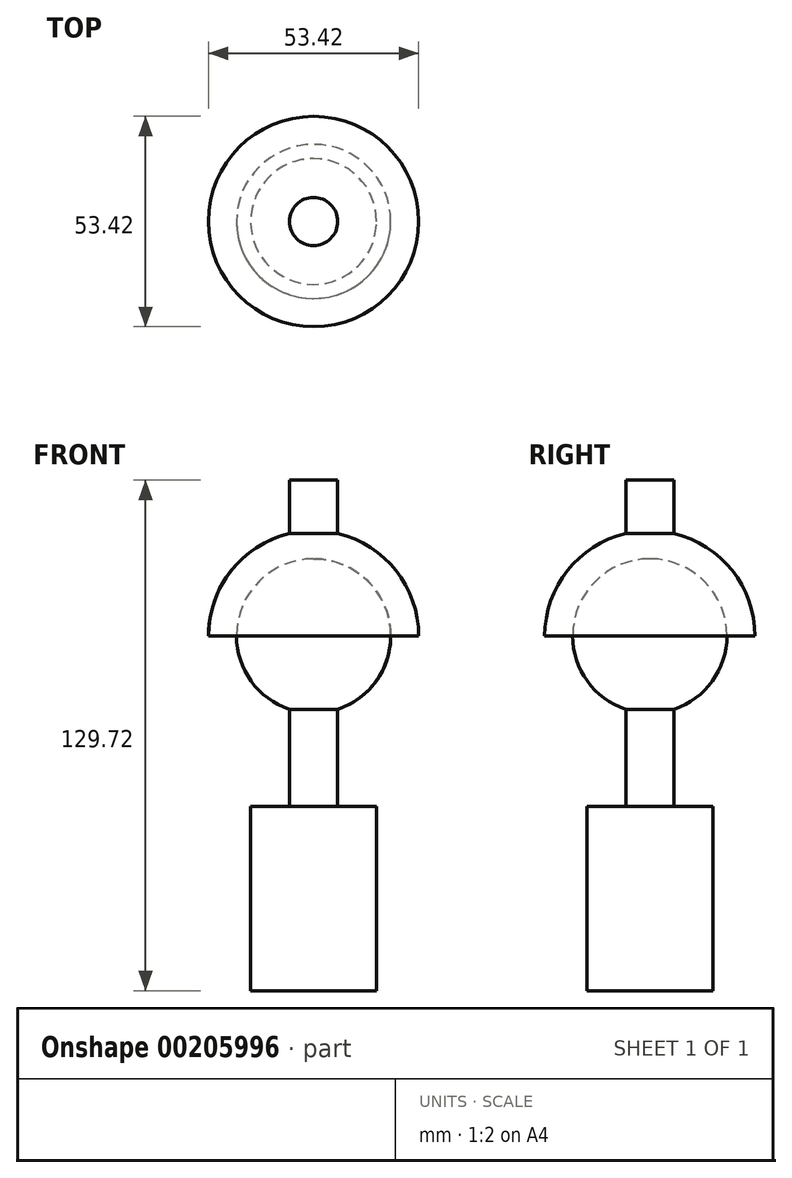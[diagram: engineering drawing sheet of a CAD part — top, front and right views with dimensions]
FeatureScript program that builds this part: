
annotation { "Feature Type Name" : "Feature", "Feature Type Description" : "" }
export const myFeature = defineFeature(function(context is Context, id is Id, definition is map)
    precondition{}
    {
        {
            var Q0;
            Q0=qCreatedBy(makeId("Front.planeOp"),FACE);
            var sketch = newSketch(context, id + "F0", { "sketchPlane" : qUnion([Q0])});
            skArc(sketch, "E0", {"start": v(6.12, 4.01) * mm, "mid": v(19.35, 25.73) * mm, "end": v(0, 42.22) * mm});
            skLineSegment(sketch, "E1.right", {"start": v(6.12, 4.01) * mm, "end": v(6.12, -20.67) * mm});
            skPoint(sketch, "E1.middle", {"position": v(0, -7.47) * mm});
            skLineSegment(sketch, "E2", {"start": v(6.12, -20.67) * mm, "end": v(15.99, -20.67) * mm});
            skLineSegment(sketch, "E3", {"start": v(15.99, -20.67) * mm, "end": v(15.99, -67.5) * mm});
            skLineSegment(sketch, "E4", {"start": v(15.99, -67.5) * mm, "end": v(0, -67.5) * mm});
            skLineSegment(sketch, "E5", {"start": v(0, -67.5) * mm, "end": v(0, 42.22) * mm});
            skPoint(sketch, "E6.orphan", {"position": v(-6.12, -20.67) * mm});
            skPoint(sketch, "E1.left.start.orphan", {"position": v(-6.12, 5.73) * mm});
            skPoint(sketch, "E7.orphan", {"position": v(6.12, 5.73) * mm});
            skArc(sketch, "E8.0", {"start": v(26.7, 22.63) * mm, "mid": v(20.94, 39.2) * mm, "end": v(6.12, 48.62) * mm});
            skLineSegment(sketch, "E9", {"start": v(0, 42.22) * mm, "end": v(0, 49.34) * mm});
            skLineSegment(sketch, "E10", {"start": v(6.12, 48.62) * mm, "end": v(6.12, 62.22) * mm});
            skLineSegment(sketch, "E11", {"start": v(6.12, 62.22) * mm, "end": v(0, 62.22) * mm});
            skLineSegment(sketch, "E12", {"start": v(0, 62.22) * mm, "end": v(0, 49.34) * mm});
            skLineSegment(sketch, "E13", {"start": v(19.6, 22.63) * mm, "end": v(26.7, 22.63) * mm});
            skLineSegment(sketch, "E14", {"start": v(0, 22.63) * mm, "end": v(29.71, 22.63) * mm, "construction": true});
            skSolve(sketch);
        }
        {
            var Q0;
            Q0=makeQuery(id+"F0.imprint","IMPRINT",FACE,{"disambiguationData":[TD([[makeQuery(id+"F0.imprint","IMPRINT",EDGE,{"derivedFrom":sQuery(id+"F0.wireOp",EDGE,"E0")}),1.0]])]});
            var Q1;
            Q1=sQuery(id+"F0.wireOp",EDGE,"E5");
            revolve(context, id + "F1", {"entities" : qUnion([Q0]), "axis" : qUnion([Q1]), "revolveType" : RevolveType.FULL});
        }
        {
            var Q0;
            Q0=makeQuery(id+"F0.imprint","IMPRINT",FACE,{"disambiguationData":[TD([[makeQuery(id+"F0.imprint","IMPRINT",EDGE,{"derivedFrom":sQuery(id+"F0.wireOp",EDGE,"E0")}),-1.0]])]});
            var Q1;
            Q1=sQuery(id+"F0.wireOp",EDGE,"E9");
            revolve(context, id + "F2", {"entities" : qUnion([Q0]), "axis" : qUnion([Q1]), "revolveType" : RevolveType.FULL});
        }
    });
